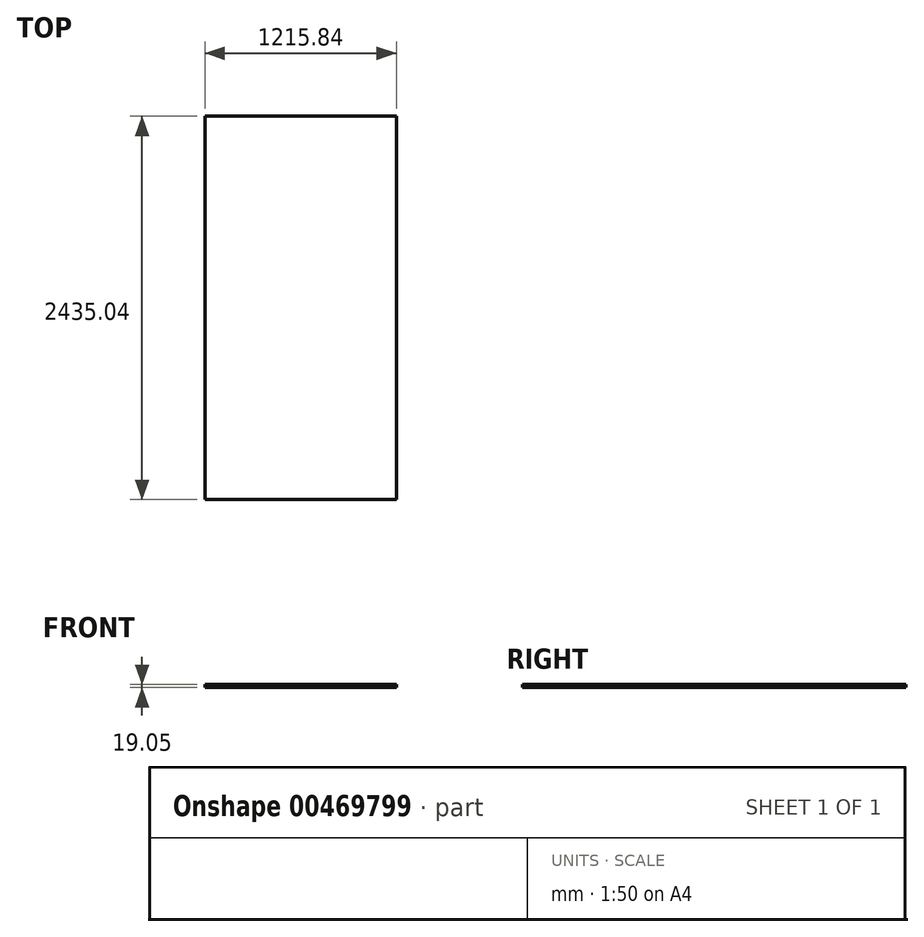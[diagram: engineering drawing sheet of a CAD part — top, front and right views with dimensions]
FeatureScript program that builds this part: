
annotation { "Feature Type Name" : "Feature", "Feature Type Description" : "" }
export const myFeature = defineFeature(function(context is Context, id is Id, definition is map)
    precondition{}
    {
        {
            var Q0;
            Q0=qCreatedBy(makeId("Top.planeOp"),FACE);
            var sketch = newSketch(context, id + "F0", { "sketchPlane" : qUnion([Q0])});
            skLineSegment(sketch, "E0.bottom", {"start": v(-607.92, -1217.52) * mm, "end": v(607.92, -1217.52) * mm});
            skLineSegment(sketch, "E0.top", {"start": v(-607.92, 1217.52) * mm, "end": v(607.92, 1217.52) * mm});
            skLineSegment(sketch, "E0.left", {"start": v(-607.92, -1217.52) * mm, "end": v(-607.92, 1217.52) * mm});
            skLineSegment(sketch, "E0.right", {"start": v(607.92, -1217.52) * mm, "end": v(607.92, 1217.52) * mm});
            skPoint(sketch, "E0.middle", {"position": v(0, 0) * mm});
            skSolve(sketch);
        }
        {
            var Q0;
            Q0=qSketchRegion(id+"F0",true);
            extrude(context, id + "F1", {"entities" : qUnion([Q0]), "depth" : 19.05 * mm});
        }
    });
